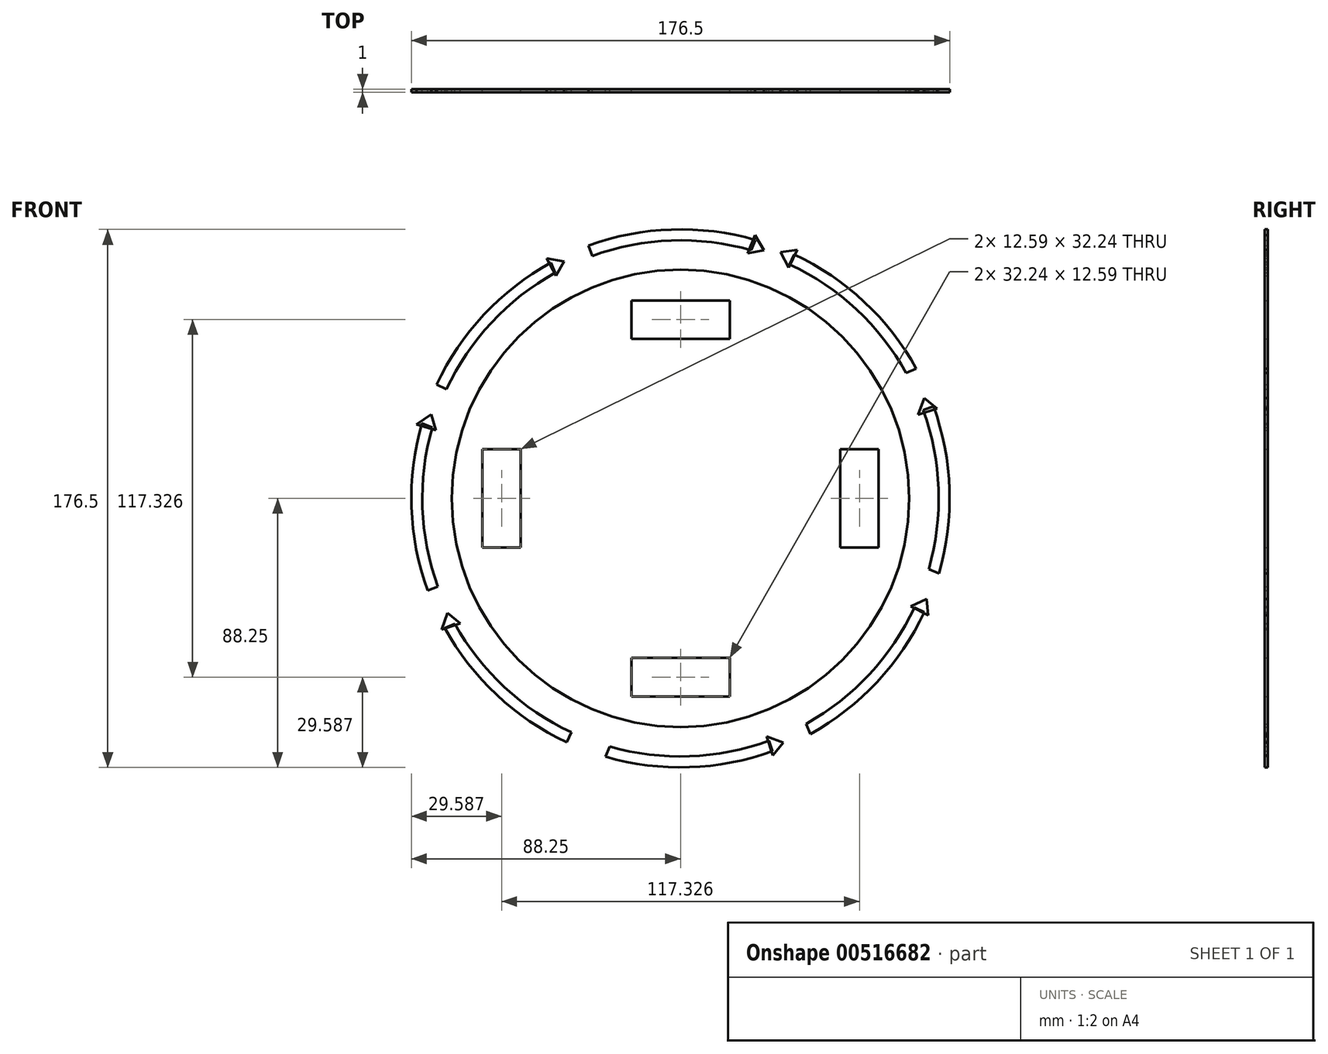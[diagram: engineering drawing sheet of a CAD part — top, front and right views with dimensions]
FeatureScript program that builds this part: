
annotation { "Feature Type Name" : "Feature", "Feature Type Description" : "" }
export const myFeature = defineFeature(function(context is Context, id is Id, definition is map)
    precondition{}
    {
        {
            var Q0;
            Q0=qCreatedBy(makeId("Front.planeOp"),FACE);
            var sketch = newSketch(context, id + "F0", { "sketchPlane" : qUnion([Q0])});
            skCircle(sketch, "E0", {"center": v(0, 0) * mm, "radius": 75 * mm});
            skSolve(sketch);
        }
        {
            var Q0;
            Q0=qCreatedBy(makeId("Front.planeOp"),FACE);
            var sketch = newSketch(context, id + "F1", { "sketchPlane" : qUnion([Q0])});
            skArc(sketch, "E1", {"start": v(23.21, 81.42) * mm, "mid": v(-3.02, 84.6) * mm, "end": v(-28.96, 79.56) * mm});
            skArc(sketch, "E2", {"start": v(24.6, 84.75) * mm, "mid": v(-2.94, 88.2) * mm, "end": v(-30.18, 82.93) * mm});
            skLineSegment(sketch, "E3.MirrorCS", {"start": v(-28.96, 79.56) * mm, "end": v(-30.18, 82.93) * mm});
            skLineSegment(sketch, "E4", {"start": v(24.6, 84.75) * mm, "end": v(23.21, 81.42) * mm});
            skSolve(sketch);
        }
        {
            var Q0;
            Q0 = qSketchRegion(id + "F1", true);
            extrude(context, id + "F2", {"entities" : qUnion([Q0]), "depth" : 1 * mm, "offsetDistance" : 25 * mm});
        }
        {
            var Q0;
            Q0 = qSketchRegion(id + "F0", true);
            extrude(context, id + "F3", {"entities" : qUnion([Q0]), "depth" : 1 * mm, "offsetDistance" : 25 * mm});
        }
        {
            var Q0;
            Q0=makeQuery(id+"F2.opExtrude","SWEPT_BODY",BODY,{"disambiguationData":[OSD([sQuery(id+"F1.wireOp",EDGE,"E1"),sQuery(id+"F1.wireOp",EDGE,"E2"),sQuery(id+"F1.wireOp",EDGE,"E3.MirrorCS"),sQuery(id+"F1.wireOp",EDGE,"WQlNMBx2-C1SZ-ekE0-ngs6-iPxVDx29oBsH"),sQuery(id+"F1.wireOp",EDGE,"zJAhY9u9-8Gia-E41C-mi51-8PP97aSefjC8"),sQuery(id+"F1.wireOp",EDGE,"JtYJnc1D-7XXK-JLj0-8JkI-pbRBsOHG98ru"),sQuery(id+"F1.wireOp",EDGE,"c6571ff0-9e6b-4c6f-b682-ac1a91efdf67.trimOffspring")])]});
            var Q1;
            Q1=makeQuery(id+"F3.opExtrude","SWEPT_FACE",FACE,{"disambiguationData":[OSD([sQuery(id+"F0.wireOp",EDGE,"E0")])]});
            circularPattern(context, id + "F4", {"entities" : qUnion([Q0]), "axis" : qUnion([Q1]), "angle" : 360 * degree, "instanceCount" : 8, "equalSpace" : true});
        }
        {
            var Q0;
            Q0=qCreatedBy(makeId("Front.planeOp"),FACE);
            var sketch = newSketch(context, id + "F5", { "sketchPlane" : qUnion([Q0])});
            skLineSegment(sketch, "E5", {"start": v(27.4, 81.36) * mm, "end": v(24.46, 86.41) * mm});
            skLineSegment(sketch, "E6", {"start": v(24.46, 86.41) * mm, "end": v(22.08, 80.35) * mm});
            skLineSegment(sketch, "E7", {"start": v(22.08, 80.35) * mm, "end": v(27.4, 81.36) * mm});
            skLineSegment(sketch, "E8", {"start": v(-38.17, 77.77) * mm, "end": v(-43.92, 78.77) * mm});
            skLineSegment(sketch, "E9", {"start": v(-43.92, 78.77) * mm, "end": v(-40.81, 73.05) * mm});
            skLineSegment(sketch, "E10", {"start": v(-40.81, 73.05) * mm, "end": v(-38.17, 77.77) * mm});
            skLineSegment(sketch, "E11", {"start": v(-81.73, 27.61) * mm, "end": v(-86.5, 24.25) * mm});
            skLineSegment(sketch, "E12", {"start": v(-86.5, 24.25) * mm, "end": v(-80.26, 22.4) * mm});
            skLineSegment(sketch, "E13", {"start": v(-80.26, 22.4) * mm, "end": v(-81.73, 27.61) * mm});
            skLineSegment(sketch, "E14", {"start": v(-76.35, -37.61) * mm, "end": v(-78.34, -43.1) * mm});
            skLineSegment(sketch, "E15", {"start": v(-78.34, -43.1) * mm, "end": v(-72.16, -41.03) * mm});
            skLineSegment(sketch, "E16", {"start": v(-72.16, -41.03) * mm, "end": v(-76.35, -37.61) * mm});
            skLineSegment(sketch, "E17", {"start": v(32.86, 80.84) * mm, "end": v(35.52, 75.64) * mm});
            skLineSegment(sketch, "E18", {"start": v(35.52, 75.64) * mm, "end": v(38.22, 81.57) * mm});
            skLineSegment(sketch, "E19", {"start": v(38.22, 81.57) * mm, "end": v(32.86, 80.84) * mm});
            skLineSegment(sketch, "E20", {"start": v(79.92, 32.9) * mm, "end": v(77.93, 27.41) * mm});
            skLineSegment(sketch, "E21", {"start": v(77.93, 27.41) * mm, "end": v(84.1, 29.48) * mm});
            skLineSegment(sketch, "E22", {"start": v(84.1, 29.48) * mm, "end": v(79.92, 32.9) * mm});
            skLineSegment(sketch, "E23", {"start": v(80.71, -33) * mm, "end": v(75.43, -35.47) * mm});
            skLineSegment(sketch, "E24", {"start": v(75.43, -35.47) * mm, "end": v(81.26, -38.38) * mm});
            skLineSegment(sketch, "E25", {"start": v(81.26, -38.38) * mm, "end": v(80.71, -33) * mm});
            skLineSegment(sketch, "E26", {"start": v(33.73, -80.1) * mm, "end": v(28.24, -78.1) * mm});
            skLineSegment(sketch, "E27", {"start": v(28.24, -78.1) * mm, "end": v(30.3, -84.29) * mm});
            skLineSegment(sketch, "E28", {"start": v(30.3, -84.29) * mm, "end": v(33.73, -80.1) * mm});
            skSolve(sketch);
        }
        {
            var Q0;
            Q0 = qSketchRegion(id + "F5", true);
            extrude(context, id + "F6", {"entities" : qUnion([Q0]), "depth" : 1 * mm, "offsetDistance" : 25 * mm});
        }
        {
            var Q0;
            Q0=qCreatedBy(makeId("Front.planeOp"),FACE);
            var sketch = newSketch(context, id + "F7", { "sketchPlane" : qUnion([Q0])});
            skLineSegment(sketch, "E29.bottom", {"start": v(-52.37, -16.12) * mm, "end": v(-64.96, -16.12) * mm});
            skLineSegment(sketch, "E29.top", {"start": v(-52.37, 16.12) * mm, "end": v(-64.96, 16.12) * mm});
            skLineSegment(sketch, "E29.left", {"start": v(-52.37, -16.12) * mm, "end": v(-52.37, 16.12) * mm});
            skLineSegment(sketch, "E29.right", {"start": v(-64.96, -16.12) * mm, "end": v(-64.96, 16.12) * mm});
            skPoint(sketch, "E29.middle", {"position": v(-58.66, 0) * mm});
            skLineSegment(sketch, "E30.left", {"start": v(-52.37, 0) * mm, "end": v(-52.37, 0) * mm});
            skLineSegment(sketch, "E30.right", {"start": v(-64.96, 0) * mm, "end": v(-64.96, 0) * mm});
            skLineSegment(sketch, "E31.1.0", {"start": v(-16.12, -52.37) * mm, "end": v(-16.12, -64.96) * mm});
            skLineSegment(sketch, "E31.1.1", {"start": v(16.12, -52.37) * mm, "end": v(-16.12, -52.37) * mm});
            skLineSegment(sketch, "E31.1.2", {"start": v(16.12, -52.37) * mm, "end": v(16.12, -64.96) * mm});
            skLineSegment(sketch, "E31.1.3", {"start": v(16.12, -64.96) * mm, "end": v(-16.12, -64.96) * mm});
            skLineSegment(sketch, "E31.2.0", {"start": v(52.37, -16.12) * mm, "end": v(64.96, -16.12) * mm});
            skLineSegment(sketch, "E31.2.1", {"start": v(52.37, 16.12) * mm, "end": v(52.37, -16.12) * mm});
            skLineSegment(sketch, "E31.2.2", {"start": v(52.37, 16.12) * mm, "end": v(64.96, 16.12) * mm});
            skLineSegment(sketch, "E31.2.3", {"start": v(64.96, 16.12) * mm, "end": v(64.96, -16.12) * mm});
            skLineSegment(sketch, "E31.3.0", {"start": v(16.12, 52.37) * mm, "end": v(16.12, 64.96) * mm});
            skLineSegment(sketch, "E31.3.1", {"start": v(-16.12, 52.37) * mm, "end": v(16.12, 52.37) * mm});
            skLineSegment(sketch, "E31.3.2", {"start": v(-16.12, 52.37) * mm, "end": v(-16.12, 64.96) * mm});
            skLineSegment(sketch, "E31.3.3", {"start": v(-16.12, 64.96) * mm, "end": v(16.12, 64.96) * mm});
            skPoint(sketch, "E31.center", {"position": v(0, 0) * mm});
            skSolve(sketch);
        }
        {
            var Q0;
            Q0 = qSketchRegion(id + "F7", true);
            extrude(context, id + "F8", {"entities" : qUnion([Q0]), "operationType" : NewBodyOperationType.REMOVE, "depth" : 1 * mm, "offsetDistance" : 25 * mm});
        }
    });
